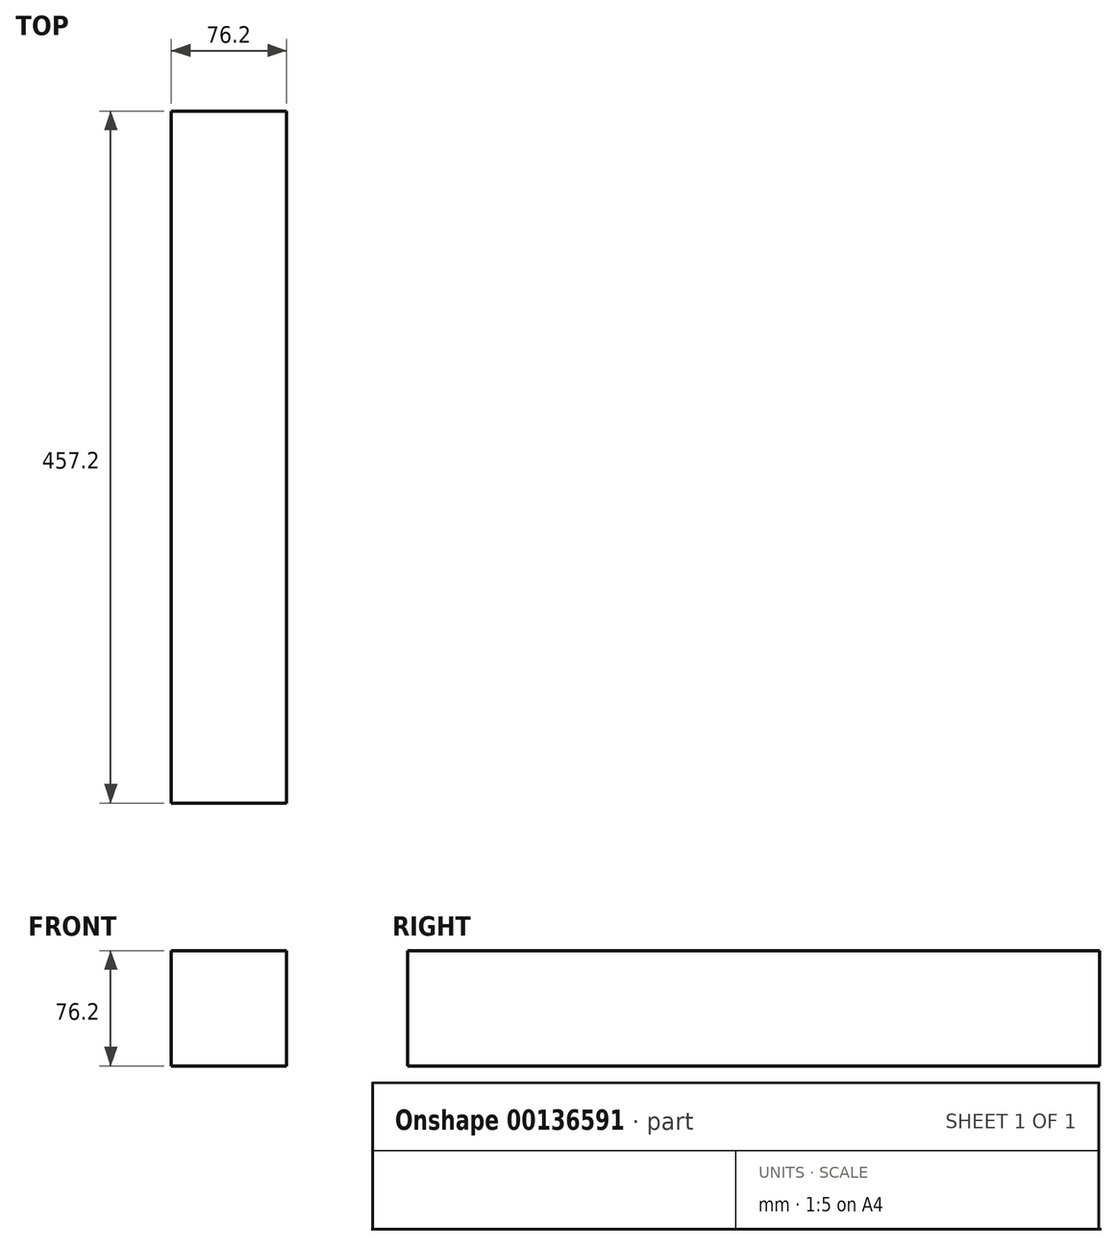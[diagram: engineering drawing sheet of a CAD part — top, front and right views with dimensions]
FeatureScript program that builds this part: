
annotation { "Feature Type Name" : "Feature", "Feature Type Description" : "" }
export const myFeature = defineFeature(function(context is Context, id is Id, definition is map)
    precondition{}
    {
        {
            var Q0;
            Q0=qCreatedBy(makeId("Front.planeOp"),FACE);
            var sketch = newSketch(context, id + "F0", { "sketchPlane" : qUnion([Q0])});
            skLineSegment(sketch, "E0.bottom", {"start": v(0, 0) * mm, "end": v(76.2, 0) * mm});
            skLineSegment(sketch, "E0.top", {"start": v(0, 76.2) * mm, "end": v(76.2, 76.2) * mm});
            skLineSegment(sketch, "E0.left", {"start": v(0, 0) * mm, "end": v(0, 76.2) * mm});
            skLineSegment(sketch, "E0.right", {"start": v(76.2, 0) * mm, "end": v(76.2, 76.2) * mm});
            skSolve(sketch);
        }
        {
            var Q0;
            Q0=makeQuery(id+"F0.imprint","IMPRINT",FACE,{"disambiguationData":[TD([[makeQuery(id+"F0.imprint","IMPRINT",EDGE,{"derivedFrom":sQuery(id+"F0.wireOp",EDGE,"E0.bottom")}),1.0]])]});
            extrude(context, id + "F1", {"entities" : qUnion([Q0]), "depth" : 457.2 * mm});
        }
    });
